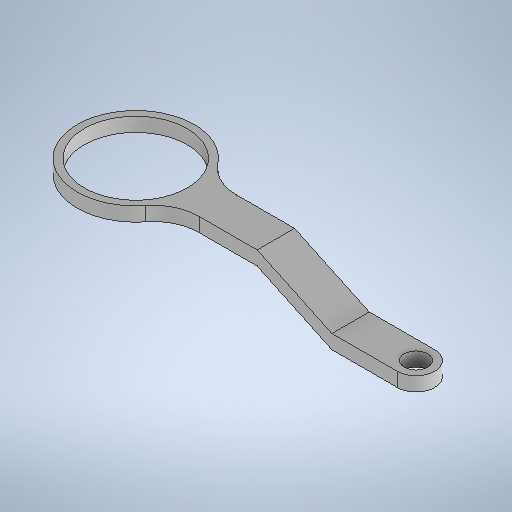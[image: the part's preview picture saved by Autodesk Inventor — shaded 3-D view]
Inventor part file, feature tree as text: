
AUTODESK INVENTOR PART (.ipt)
format: ipt  version: 2025.1 (Build 291241000, 241)  size: 297,472 bytes
history: native  units: mm
features: sketch x4, extrude x3, plane x1, hole x1
ambient origin geometry x8: Origin, YZ Plane, XZ Plane, XY Plane, X Axis, Y Axis, Z Axis, Center Point
bodies: Solid1 (feature_tree)
feature tree (9):
  sketch  "Sketch1"  dims[d0=25.0mm d1=22.0mm]
  extrude  "Extrusion1"  Depth=22.0mm
  plane  "Work Plane3"
  extrude  "Extrusion3"  Depth=10.0mm
  extrude  "Extrusion4"  Depth=3.0mm TaperAngle=0.0deg
  hole  "Hole1"  [1 undecoded]
  sketch  "Sketch7"  dims[d2=4.0mm d3=10.0mm]
  sketch  "Sketch8"  dims[d4=60.0mm d5=3.0mm d6=0.0mm]
  sketch  "Sketch9"  dims[d17=42.5mm d18=0.0mm d19=7.5mm d20=14.0mm d21=60.0mm d22=3.0mm d23=8.0mm d24=0.0mm d25=4.0mm d26=8.0mm d27=0.0mm d28=5.0mm d29=6.0mm d30=4.0mm d31=2.0mm d32=90.0deg d33=8.0mm d34=0.0mm]
note: 1 required parameter value undecoded (feature->parameter linkage not recoverable at this tier; creation-order binding heuristic only, values carry confidence <= 0.55)
